# Revit family: ALABAX LG
name_source: partatom
category: Lighting Fixtures
revit_build: Autodesk Revit 2017 (Build: 20181011_1645(x64)
units: mm (PartAtom-declared; Revit-internal decimal feet)

## family parameters
Cut with Voids When Loaded = No
Host = Face
Light Source = Yes
Part Type = Normal
Room Calculation Point = No
Round Connector Dimension = Use Diameter
Shared = Yes

## types (1)
- Black
    Canopy Width = 0' - 5 3/4"
    Color Filter = 16777215
    Cost = 189 $
    Default Elevation = 4' - 0"
    Description = Using simple, tulip-like silhouettes originally found in fixtures from a 1951 General Electric industrial catalog, the Alabax Collection celebrates the functional artistry of utilitarian lighting. Each fixture is expertly cast and glazed by hand in Portland, Oregon. The selection of custom glaze tones range from cleanly institutional to eye-catching and energetic. Finished to your specifications and assembled by hand in our Portland factory. A Schoolhouse Original.
    Dimming Lamp Color Temperature Shift = <None>
    Emit Shape Visible in Rendering = No
    Emit from Circle Diameter = 2' - 0"
    Height = 0' - 7"
    Length = 0' - 7"
    Light Source Symbol Size = 2' - 0"
    Manufacturer = Schoolhouse
    Max Wattage = 150 W
    Model = Alabax Large
    Primary Finishes = Schoolhouse Black 0-0-0
    Product Material = Ceramic
    URL = https://www.schoolhouse.com
    Voltage = 120/220V
    Width = 0' - 8 1/2"

## geometry (parser evidence)
native form markers: Sweep x9
no freeform markers — native parametric forms only
